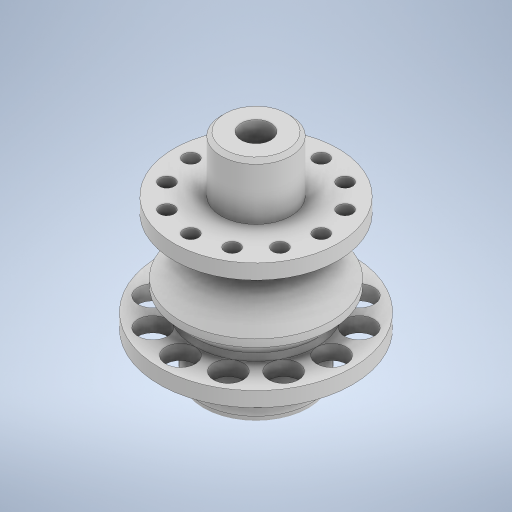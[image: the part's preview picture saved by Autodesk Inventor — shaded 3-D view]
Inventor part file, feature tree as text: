
AUTODESK INVENTOR PART (.ipt)
format: ipt  version: 2023.2 (Build 272271000, 271)  size: 715,776 bytes
history: native  units: mm
features: extrude x6, sketch x5, pattern_circular x3, fillet x3, other x2, revolve x2, chamfer x1
ambient origin geometry x8: Origin, YZ Plane, XZ Plane, XY Plane, X Axis, Y Axis, Z Axis, Center Point
bodies: Body1 (feature_tree)
feature tree (22):
  other  "Твердое тело1"
  extrude  "Выдавливание1"  Depth=14.7mm
  extrude  "Выдавливание2"  Depth=2.0mm TaperAngle=0.0deg
  other  "РабПлоскость1"
  extrude  "Выдавливание3"  Depth=12.0mm
  pattern_circular  "Круговой массив1"  [2 undecoded]
  extrude  "Выдавливание4"  Depth=7.35mm
  extrude  "Выдавливание5"  Depth=2.0mm
  pattern_circular  "Круговой массив2"  [2 undecoded]
  revolve  "Вращение1"
  extrude  "Выдавливание6"  Depth=3.0mm TaperAngle=0.0deg
  pattern_circular  "Круговой массив3"  Count=8 Angle=360.0deg
  revolve  "Вращение2"
  chamfer  "Фаска2"  Distance=26.0mm
  fillet  "Сопряжение1"  Radius=2.0mm
  fillet  "Сопряжение2"  Radius=4.0mm
  fillet  "Сопряжение3"  Radius=2.0mm
  sketch  "Эскиз1"
  sketch  "Эскиз2"
  sketch  "Эскиз3"
  sketch  "Эскиз4"
  sketch  "Эскиз9"
note: 4 required parameter values undecoded (feature->parameter linkage not recoverable at this tier; creation-order binding heuristic only, values carry confidence <= 0.55)
